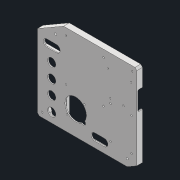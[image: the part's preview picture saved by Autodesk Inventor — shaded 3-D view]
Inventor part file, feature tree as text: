
AUTODESK INVENTOR PART (.ipt)
format: ipt  version: 2022 (Build 260153000, 153)  size: 531,456 bytes
history: native  units: mm
features: reference x18, sketch x10, extrude x9, other x7, fillet x5, hole x4, projected_geometry x3, imported_body x1, chamfer x1
ambient origin geometry x8: Origin, YZ Plane, XZ Plane, XY Plane, X Axis, Y Axis, Z Axis, Center Point
bodies: Solid1 (feature_tree)
feature tree (58):
  imported_body  "BASE"
  extrude  "Extrusion1"  Depth=150.0mm
  extrude  "Extrusion2"  Depth=10.0mm
  fillet  "Fillet1"  Radius=200.0mm
  hole  "Hole1"  [1 undecoded]
  hole  "wall mount"  [1 undecoded]
  hole  "cover mount"  [1 undecoded]
  chamfer  "Chamfer1"  Distance=2.0mm Angle=45.0deg
  extrude  "Extrusion4"  Depth=2.0mm
  extrude  "Extrusion5"  Depth=2.0mm
  hole  "Hole4"  [1 undecoded]
  extrude  "speaker"  Depth=2.0mm
  sketch  "Sketch19"  dims[d75=10.0mm]
  extrude  "Extrusion8"  Depth=2.0mm
  fillet  "Fillet3"  Radius=6.5mm
  fillet  "Fillet2"  Radius=6.5mm
  extrude  "Extrusion10"  Depth=10.0mm TaperAngle=0.0deg
  extrude  "Extrusion7"  Depth=2.0mm
  extrude  "Extrusion11"  Depth=2.0mm
  fillet  "Fillet4"  Radius=80.0mm
  fillet  "Fillet5"  [1 undecoded]
  sketch  "Sketch23"  dims[d77=10.0mm d78=4.0mm d79=2.0mm d80=45.0deg d81=5.0mm d82=5.0mm d83=10.0mm d84=0.0mm d89=16.0mm d90=16.0mm d91=6.5mm d92=6.5mm d93=10.0mm d94=0.0mm d95=45.0mm d96=50.0mm d97=80.0mm d98=0.0mm d99=0.0mm d100=3.6mm d101=6.0mm d102=6.5mm d103=3.4mm d104=90.0deg d105=8.0mm d106=20.594885mm d107=5.0mm d108=15.0mm d109=20.0mm d110=130.0mm d111=20.0mm d112=10.0mm d113=0.0mm d116=150.0mm d117=150.0mm d118=20.0mm d119=15.0mm d120=30.0mm d121=140.0mm d122=4.0mm d123=60.0deg d124=60.0deg d125=4.0mm d126=15.0mm d127=20.0mm d135=10.0mm d136=0.0mm d137=4.0mm d141=3.0mm d142=120.0mm d143=52.0mm d148=9.0mm d149=0.0mm d150=0.0mm d151=40.0mm d152=40.0mm d153=40.0mm d154=40.0mm d155=8.0mm d156=0.0mm d157=3.0mm d158=9.0mm d159=9.0mm d160=9.0mm d161=2.0mm d162=9.0mm d163=0.5mm d164=0.872665mm d165=0.5mm d166=0.872665mm]
  sketch  "Sketch9"  dims[d4=60.0deg d5=150.0mm]
  reference  "Reference13"
  reference  "Reference14"
  reference  "Reference15"
  reference  "Reference16"
  reference  "Reference17"
  reference  "Reference18"
  reference  "Reference19"
  reference  "Reference20"
  reference  "Reference21"
  reference  "Reference22"
  projected_geometry  "Projected Loop2"
  reference  "Reference23"
  reference  "Reference24"
  sketch  "Sketch10"  dims[d6=10.0mm d7=180.0mm d8=200.0mm]
  projected_geometry  "Projected Loop3"
  sketch  "Sketch11"  dims[d10=2.0mm d11=2.0mm d12=0.0mm]
  sketch  "Sketch12"  dims[d13=2.0mm d14=0.0mm d19=10.0mm d20=0.0mm]
  sketch  "Sketch15"  dims[d49=3.6mm d50=6.0mm d51=6.5mm d52=3.4mm d53=90.0deg d54=8.0mm d55=20.594885mm]
  sketch  "Sketch16"  dims[d60=4.8mm d61=6.0mm d62=8.0mm d63=4.6mm d64=90.0deg d65=8.0mm d66=20.594885mm]
  reference  "Reference25"
  reference  "Reference26"
  sketch  "Sketch17"  dims[d67=3.6mm d68=6.0mm d69=6.5mm d70=3.4mm d71=90.0deg d72=8.0mm d73=20.594885mm d74=10.0mm]
  projected_geometry  "Projected Loop4"
  sketch  "Sketch22"  dims[d76=10.0mm]
  reference  "Reference28"
  reference  "Reference29"
  reference  "Reference30"
  reference  "Reference31"
  parser-record x1  (decoder bookkeeping rows leaked as tree rows — omitted from the tree; the rows remain in map.json)
  other  "Ensamble.iam"
  other  "mainboard:1"
  other  "4_Relay_module_Simplify_1:1"
  other  "Ardi_UNO:1"
  other  "speaker:1"
  other  "Cubierta:1"
note: 5 required parameter values undecoded (feature->parameter linkage not recoverable at this tier; creation-order binding heuristic only, values carry confidence <= 0.55)
note: 1 file-system path scrubbed to <path> (originals preserved in map.json)
